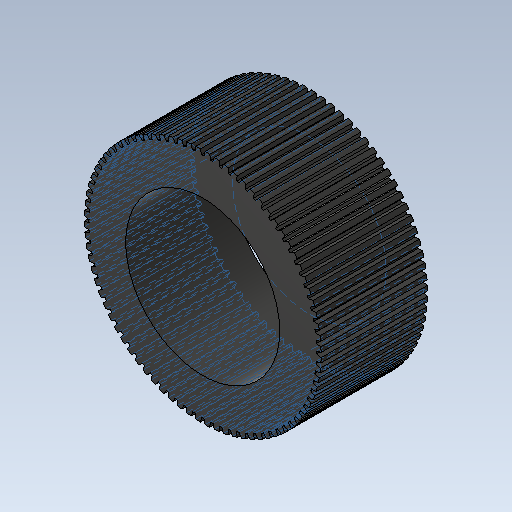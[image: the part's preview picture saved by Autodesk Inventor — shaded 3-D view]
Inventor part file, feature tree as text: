
AUTODESK INVENTOR PART (.ipt)
format: ipt  version: 2020 (Build 240168000, 168)  size: 583,680 bytes
history: native  units: mm
features: extrude x3, sketch x3, other x1
ambient origin geometry x8: Origin, YZ Plane, XZ Plane, XY Plane, X Axis, Y Axis, Z Axis, Center Point
bodies: Body1 (feature_tree)
feature tree (7):
  other  "ソリッド1"
  extrude  "押し出し1"  Depth=10.0mm
  extrude  "押し出し2"  Depth=4.5mm TaperAngle=0.0deg
  extrude  "押し出し3"  Depth=6.5mm
  sketch  "スケッチ1"
  sketch  "スケッチ2"
  sketch  "スケッチ3"
